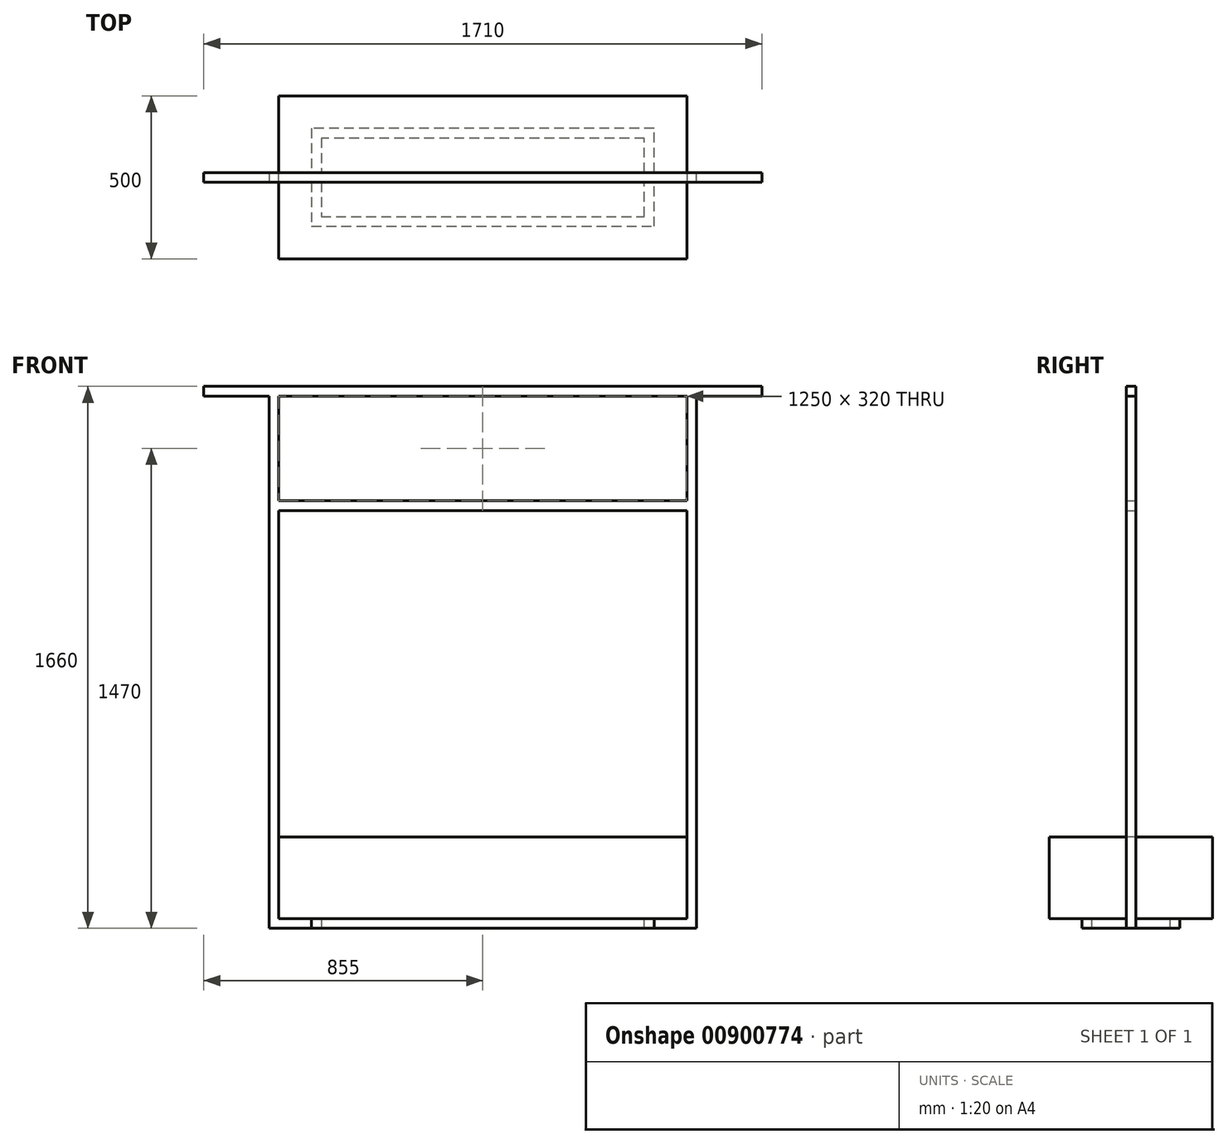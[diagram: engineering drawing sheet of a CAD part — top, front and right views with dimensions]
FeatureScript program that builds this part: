
annotation { "Feature Type Name" : "Feature", "Feature Type Description" : "" }
export const myFeature = defineFeature(function(context is Context, id is Id, definition is map)
    precondition{}
    {
        {
            var Q0;
            Q0=qCreatedBy(makeId("Top.planeOp"),FACE);
            var sketch = newSketch(context, id + "F0", { "sketchPlane" : qUnion([Q0])});
            skLineSegment(sketch, "E0.bottom", {"start": v(-625, 250) * mm, "end": v(625, 250) * mm});
            skLineSegment(sketch, "E0.top", {"start": v(-625, -250) * mm, "end": v(625, -250) * mm});
            skLineSegment(sketch, "E0.left", {"start": v(-625, 250) * mm, "end": v(-625, -250) * mm});
            skLineSegment(sketch, "E0.right", {"start": v(625, 250) * mm, "end": v(625, -250) * mm});
            skLineSegment(sketch, "E1", {"start": v(-625, 250) * mm, "end": v(625, -250) * mm, "construction": true});
            skSolve(sketch);
        }
        {
            var Q0;
            Q0=qSketchRegion(id+"F0",true);
            extrude(context, id + "F1", {"entities" : qUnion([Q0]), "depth" : 250 * mm, "offsetDistance" : 25 * mm});
        }
        {
            var Q0;
            Q0=qCreatedBy(makeId("Front.planeOp"),FACE);
            var sketch = newSketch(context, id + "F2", { "sketchPlane" : qUnion([Q0])});
            skLineSegment(sketch, "E2", {"start": v(625, 0) * mm, "end": v(625, 1600) * mm});
            skLineSegment(sketch, "E3", {"start": v(625, 1600) * mm, "end": v(-625, 1600) * mm});
            skLineSegment(sketch, "E4", {"start": v(-625, 1600) * mm, "end": v(-625, 0) * mm});
            skLineSegment(sketch, "E5", {"start": v(-625, 0) * mm, "end": v(625, 0) * mm});
            skLineSegment(sketch, "E6.0", {"start": v(655, 1630) * mm, "end": v(-655, 1630) * mm});
            skLineSegment(sketch, "E6.1", {"start": v(655, -30) * mm, "end": v(655, 1630) * mm});
            skLineSegment(sketch, "E6.2", {"start": v(-655, -30) * mm, "end": v(655, -30) * mm});
            skLineSegment(sketch, "E6.3", {"start": v(-655, 1630) * mm, "end": v(-655, -30) * mm});
            skSolve(sketch);
        }
        {
            var Q0;
            Q0=qSketchRegion(id+"F2",true);
            extrude(context, id + "F3", {"entities" : qUnion([Q0]), "endBound" : BoundingType.SYMMETRIC, "depth" : 30 * mm, "offsetDistance" : 25 * mm});
        }
        {
            var Q0;
            Q0=makeQuery(id+"F1.opExtrude","CAP_FACE",FACE,{"disambiguationData":[OSD([sQuery(id+"F0.wireOp",EDGE,"E0.bottom"),sQuery(id+"F0.wireOp",EDGE,"E0.top"),sQuery(id+"F0.wireOp",EDGE,"E0.left"),sQuery(id+"F0.wireOp",EDGE,"E0.right")])],"isStart":true});
            var sketch = newSketch(context, id + "F4", { "sketchPlane" : qUnion([Q0])});
            skLineSegment(sketch, "E7", {"start": v(525, 150) * mm, "end": v(525, -150) * mm});
            skLineSegment(sketch, "E8", {"start": v(525, -150) * mm, "end": v(-525, -150) * mm});
            skLineSegment(sketch, "E9", {"start": v(-525, -150) * mm, "end": v(-525, 150) * mm});
            skLineSegment(sketch, "E10", {"start": v(-525, 150) * mm, "end": v(525, 150) * mm});
            skLineSegment(sketch, "E11.0", {"start": v(-495, 120) * mm, "end": v(495, 120) * mm});
            skLineSegment(sketch, "E11.1", {"start": v(-495, -120) * mm, "end": v(-495, 120) * mm});
            skLineSegment(sketch, "E11.2", {"start": v(495, -120) * mm, "end": v(-495, -120) * mm});
            skLineSegment(sketch, "E11.3", {"start": v(495, 120) * mm, "end": v(495, -120) * mm});
            skSolve(sketch);
        }
        {
            var Q0;
            Q0=qSketchRegion(id+"F4",true);
            extrude(context, id + "F5", {"entities" : qUnion([Q0]), "operationType" : NewBodyOperationType.ADD, "depth" : 30 * mm, "offsetDistance" : 25 * mm});
        }
        {
            var Q0;
            Q0=makeQuery(id+"F3.opExtrude","SWEPT_FACE",FACE,{"disambiguationData":[OSD([sQuery(id+"F2.wireOp",EDGE,"E6.1")])]});
            var sketch = newSketch(context, id + "F6", { "sketchPlane" : qUnion([Q0])});
            skLineSegment(sketch, "E12.bottom", {"start": v(-15, 1630) * mm, "end": v(15, 1630) * mm});
            skLineSegment(sketch, "E12.top", {"start": v(-15, 1600) * mm, "end": v(15, 1600) * mm});
            skLineSegment(sketch, "E12.left", {"start": v(-15, 1630) * mm, "end": v(-15, 1600) * mm});
            skLineSegment(sketch, "E12.right", {"start": v(15, 1630) * mm, "end": v(15, 1600) * mm});
            skSolve(sketch);
        }
        {
            var Q0;
            Q0 = qSketchRegion(id + "F6", true);
            extrude(context, id + "F7", {"entities" : qUnion([Q0]), "operationType" : NewBodyOperationType.ADD, "depth" : 200 * mm, "offsetDistance" : 25 * mm});
        }
        {
            var Q0;
            Q0=makeQuery(id+"F3.opExtrude","SWEPT_FACE",FACE,{"disambiguationData":[OSD([sQuery(id+"F2.wireOp",EDGE,"E6.3")])]});
            var sketch = newSketch(context, id + "F8", { "sketchPlane" : qUnion([Q0])});
            skLineSegment(sketch, "E13.bottom", {"start": v(-15, 1630) * mm, "end": v(15, 1630) * mm});
            skLineSegment(sketch, "E13.top", {"start": v(-15, 1600) * mm, "end": v(15, 1600) * mm});
            skLineSegment(sketch, "E13.left", {"start": v(-15, 1630) * mm, "end": v(-15, 1600) * mm});
            skLineSegment(sketch, "E13.right", {"start": v(15, 1630) * mm, "end": v(15, 1600) * mm});
            skSolve(sketch);
        }
        {
            var Q0;
            Q0 = qSketchRegion(id + "F8", true);
            extrude(context, id + "F9", {"entities" : qUnion([Q0]), "operationType" : NewBodyOperationType.ADD, "depth" : 200 * mm, "offsetDistance" : 25 * mm});
        }
        {
            var Q0;
            Q0=makeQuery(id+"F3.opExtrude","SWEPT_FACE",FACE,{"disambiguationData":[OSD([sQuery(id+"F2.wireOp",EDGE,"E4")])]});
            var sketch = newSketch(context, id + "F10", { "sketchPlane" : qUnion([Q0])});
            skLineSegment(sketch, "E14.bottom", {"start": v(-15, 1280) * mm, "end": v(15, 1280) * mm});
            skLineSegment(sketch, "E14.top", {"start": v(-15, 1250) * mm, "end": v(15, 1250) * mm});
            skLineSegment(sketch, "E14.left", {"start": v(-15, 1280) * mm, "end": v(-15, 1250) * mm});
            skLineSegment(sketch, "E14.right", {"start": v(15, 1280) * mm, "end": v(15, 1250) * mm});
            skSolve(sketch);
        }
        {
            var Q0;
            Q0 = qSketchRegion(id + "F10", true);
            var Q1;
            Q1=makeQuery(id+"F3.opExtrude","SWEPT_FACE",FACE,{"disambiguationData":[OSD([sQuery(id+"F2.wireOp",EDGE,"E2")])]});
            extrude(context, id + "F11", {"entities" : qUnion([Q0]), "operationType" : NewBodyOperationType.ADD, "endBound" : BoundingType.UP_TO_SURFACE, "depth" : 25 * mm, "endBoundEntityFace" : qUnion([Q1]), "offsetDistance" : 25 * mm});
        }
    });
